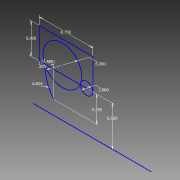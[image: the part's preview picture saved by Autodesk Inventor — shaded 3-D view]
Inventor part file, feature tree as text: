
AUTODESK INVENTOR PART (.ipt)
format: ipt  version: 2012 (Build 160160000, 160)  size: 68,608 bytes
history: native  units: in
note: dims shown in document units (in); Inventor stores cm internally (conversion verified against a paired STEP export)
features: sketch x1
ambient origin geometry x8: Origin, YZ Plane, XZ Plane, XY Plane, X Axis, Y Axis, Z Axis, Center Point
feature tree (1):
  sketch  "Sketch1"  dims[d0=6.824in d1=4.25in d2=2.0in d3=6.5in d4=6.3in d5=1.485in d6=8.75in d7=5.0in d8=0.875in]
